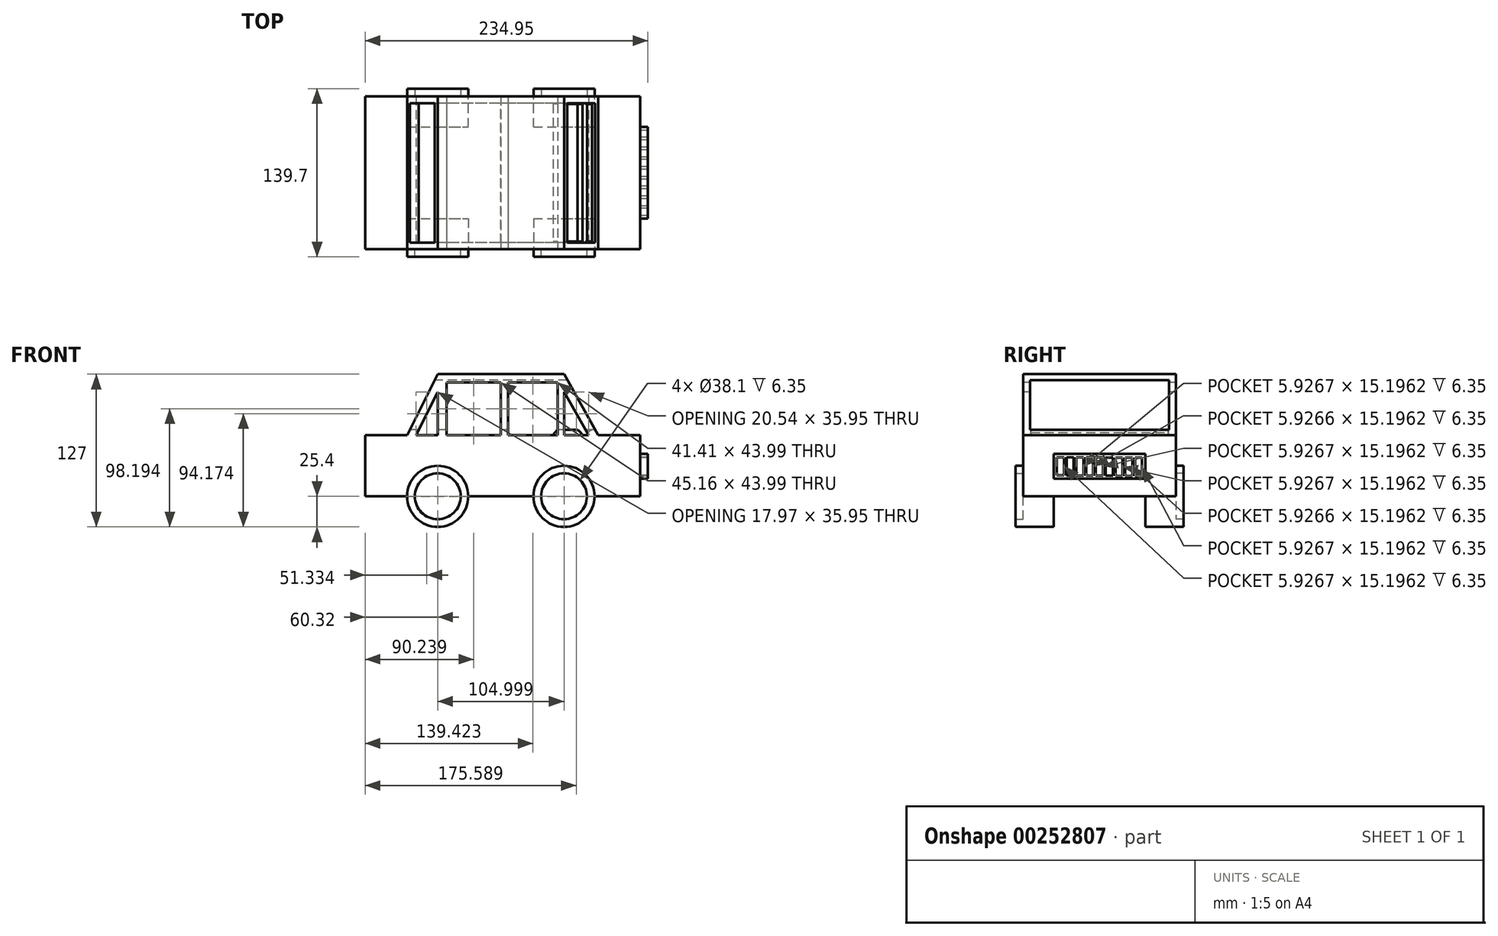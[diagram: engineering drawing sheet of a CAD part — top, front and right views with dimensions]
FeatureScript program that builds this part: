
annotation { "Feature Type Name" : "Feature", "Feature Type Description" : "" }
export const myFeature = defineFeature(function(context is Context, id is Id, definition is map)
    precondition{}
    {
        {
            var Q0;
            Q0=qCreatedBy(makeId("Front.planeOp"),FACE);
            var sketch = newSketch(context, id + "F0", { "sketchPlane" : qUnion([Q0])});
            skLineSegment(sketch, "E0.bottom", {"start": v(-112.82, 27.92) * mm, "end": v(115.78, 27.92) * mm});
            skLineSegment(sketch, "E0.top", {"start": v(-112.82, -22.88) * mm, "end": v(115.78, -22.88) * mm});
            skLineSegment(sketch, "E0.left", {"start": v(-112.82, 27.92) * mm, "end": v(-112.82, -22.88) * mm});
            skLineSegment(sketch, "E0.right", {"start": v(115.78, 27.92) * mm, "end": v(115.78, -22.88) * mm});
            skSolve(sketch);
        }
        {
            var Q0;
            Q0=makeQuery(id+"F0.imprint","IMPRINT",FACE,{"disambiguationData":[TD([[makeQuery(id+"F0.imprint","IMPRINT",EDGE,{"derivedFrom":sQuery(id+"F0.wireOp",EDGE,"E0.bottom")}),-1.0]])]});
            extrude(context, id + "F1", {"entities" : qUnion([Q0]), "endBound" : BoundingType.SYMMETRIC, "depth" : 127 * mm});
        }
        {
            var Q0;
            Q0=makeQuery(id+"F1.opExtrude","CAP_FACE",FACE,{"disambiguationData":[OSD([sQuery(id+"F0.wireOp",EDGE,"E0.bottom"),sQuery(id+"F0.wireOp",EDGE,"E0.top"),sQuery(id+"F0.wireOp",EDGE,"E0.left"),sQuery(id+"F0.wireOp",EDGE,"E0.right")])],"isStart":false});
            var sketch = newSketch(context, id + "F2", { "sketchPlane" : qUnion([Q0])});
            skCircle(sketch, "E1", {"center": v(-52.5, -22.88) * mm, "radius": 25.4 * mm});
            skLineSegment(sketch, "E2", {"start": v(-77.9, -22.88) * mm, "end": v(-112.82, -22.88) * mm});
            skCircle(sketch, "E3.MirrorC", {"center": v(52.5, -22.88) * mm, "radius": 25.4 * mm});
            skSolve(sketch);
        }
        {
            var Q0;
            Q0 = qSketchRegion(id + "F2", true);
            extrude(context, id + "F3", {"entities" : qUnion([Q0]), "operationType" : NewBodyOperationType.ADD, "oppositeDirection" : true, "depth" : 25.4 * mm});
        }
        {
            var Q0;
            Q0=makeQuery(id+"F1.opExtrude","SWEPT_BODY",BODY,{"disambiguationData":[OSD([sQuery(id+"F0.wireOp",EDGE,"E0.bottom"),sQuery(id+"F0.wireOp",EDGE,"E0.top"),sQuery(id+"F0.wireOp",EDGE,"E0.left"),sQuery(id+"F0.wireOp",EDGE,"E0.right")])]});
            var Q1;
            Q1=qCreatedBy(makeId("Front.planeOp"),FACE);
            mirror(context, id + "F4", {"operationType" : NewBodyOperationType.ADD, "entities" : qUnion([Q0]), "mirrorPlane" : qUnion([Q1])});
        }
        {
            var Q0;
            Q0=makeQuery(id+"F1.opExtrude","SWEPT_FACE",FACE,{"disambiguationData":[OSD([sQuery(id+"F0.wireOp",EDGE,"E0.bottom")])]});
            var sketch = newSketch(context, id + "F5", { "sketchPlane" : qUnion([Q0])});
            skLineSegment(sketch, "E4.bottom", {"start": v(-52.5, -63.5) * mm, "end": v(80.85, -63.5) * mm});
            skLineSegment(sketch, "E4.top", {"start": v(-52.5, 63.5) * mm, "end": v(80.85, 63.5) * mm});
            skLineSegment(sketch, "E4.left", {"start": v(-52.5, -63.5) * mm, "end": v(-52.5, 63.5) * mm});
            skLineSegment(sketch, "E4.right", {"start": v(80.85, -63.5) * mm, "end": v(80.85, 63.5) * mm});
            skLineSegment(sketch, "E5", {"start": v(-112.82, -63.5) * mm, "end": v(-52.5, -63.5) * mm});
            skSolve(sketch);
        }
        {
            var Q0;
            Q0 = qSketchRegion(id + "F5", true);
            extrude(context, id + "F6", {"entities" : qUnion([Q0]), "operationType" : NewBodyOperationType.ADD, "depth" : 50.8 * mm});
        }
        {
            var Q0;
            Q0=makeQuery(id+"F6.boolean.opBoolean","MERGE",FACE,{"derivedFrom":[makeQuery(id+"F3.boolean.opBoolean","MERGE",FACE,{"derivedFrom":[makeQuery(id+"F1.opExtrude","CAP_FACE",FACE,{"disambiguationData":[OSD([sQuery(id+"F0.wireOp",EDGE,"E0.bottom"),sQuery(id+"F0.wireOp",EDGE,"E0.top"),sQuery(id+"F0.wireOp",EDGE,"E0.left"),sQuery(id+"F0.wireOp",EDGE,"E0.right")])],"isStart":false}),makeQuery(id+"F3.opExtrude","CAP_FACE",FACE,{"disambiguationData":[OSD([sQuery(id+"F2.wireOp",EDGE,"E1")])],"isStart":true}),makeQuery(id+"F3.opExtrude","CAP_FACE",FACE,{"disambiguationData":[OSD([sQuery(id+"F2.wireOp",EDGE,"E3.MirrorC")])],"isStart":true})]}),makeQuery(id+"F6.opExtrude","SWEPT_FACE",FACE,{"disambiguationData":[OSD([sQuery(id+"F5.wireOp",EDGE,"E4.bottom")])]})]});
            var sketch = newSketch(context, id + "F7", { "sketchPlane" : qUnion([Q0])});
            skPoint(sketch, "E6.endSnap0", {"position": v(52.5, -48.28) * mm});
            skLineSegment(sketch, "E7", {"start": v(52.5, 78.72) * mm, "end": v(80.85, 27.92) * mm});
            skLineSegment(sketch, "E8", {"start": v(80.85, 78.72) * mm, "end": v(52.5, 78.72) * mm});
            skSolve(sketch);
        }
        {
            var Q0;
            Q0=makeQuery(id+"F7.imprint","IMPRINT",FACE,{"disambiguationData":[TD([[makeQuery(id+"F7.imprint","IMPRINT",EDGE,{"derivedFrom":sQuery(id+"F7.wireOp",EDGE,"E7")}),1.0]])]});
            extrude(context, id + "F8", {"entities" : qUnion([Q0]), "operationType" : NewBodyOperationType.REMOVE, "endBound" : BoundingType.THROUGH_ALL, "oppositeDirection" : true, "depth" : 25.4 * mm});
        }
        {
            var Q0;
            Q0=makeQuery(id+"F8.boolean.opBoolean","COPY",FACE,{"derivedFrom":makeQuery(id+"F8.opExtrude","SWEPT_FACE",FACE,{"disambiguationData":[OSD([sQuery(id+"F7.wireOp",EDGE,"E7")])]})});
            var sketch = newSketch(context, id + "F9", { "sketchPlane" : qUnion([Q0])});
            skLineSegment(sketch, "E9.bottom", {"start": v(-57.15, 36.8) * mm, "end": v(57.15, 36.8) * mm});
            skLineSegment(sketch, "E9.top", {"start": v(-57.15, -8.67) * mm, "end": v(57.15, -8.67) * mm});
            skLineSegment(sketch, "E9.left", {"start": v(-57.15, 36.8) * mm, "end": v(-57.15, -8.67) * mm});
            skLineSegment(sketch, "E9.right", {"start": v(57.15, 36.8) * mm, "end": v(57.15, -8.67) * mm});
            skSolve(sketch);
        }
        {
            var Q0;
            Q0=makeQuery(id+"F9.imprint","IMPRINT",FACE,{"disambiguationData":[TD([[makeQuery(id+"F9.imprint","IMPRINT",EDGE,{"derivedFrom":sQuery(id+"F9.wireOp",EDGE,"E9.bottom")}),-1.0]])]});
            extrude(context, id + "F10", {"entities" : qUnion([Q0]), "operationType" : NewBodyOperationType.REMOVE, "oppositeDirection" : true, "depth" : 25.4 * mm});
        }
        {
            var Q0;
            Q0=makeQuery(id+"F6.opExtrude","SWEPT_FACE",FACE,{"disambiguationData":[OSD([sQuery(id+"F5.wireOp",EDGE,"E4.left")])]});
            extrude(context, id + "F11", {"entities" : qUnion([Q0]), "operationType" : NewBodyOperationType.ADD, "depth" : 25.4 * mm});
        }
        {
            var Q0;
            {var subQ0=sQuery(id+"F5.wireOp",EDGE,"E4.bottom");Q0=makeQuery(id+"F11.boolean.opBoolean","MERGE",FACE,{"derivedFrom":[makeQuery(id+"F6.boolean.opBoolean","MERGE",FACE,{"derivedFrom":[makeQuery(id+"F3.boolean.opBoolean","MERGE",FACE,{"derivedFrom":[makeQuery(id+"F1.opExtrude","CAP_FACE",FACE,{"disambiguationData":[OSD([sQuery(id+"F0.wireOp",EDGE,"E0.bottom"),sQuery(id+"F0.wireOp",EDGE,"E0.top"),sQuery(id+"F0.wireOp",EDGE,"E0.left"),sQuery(id+"F0.wireOp",EDGE,"E0.right")])],"isStart":false}),makeQuery(id+"F3.opExtrude","CAP_FACE",FACE,{"disambiguationData":[OSD([sQuery(id+"F2.wireOp",EDGE,"E1")])],"isStart":true}),makeQuery(id+"F3.opExtrude","CAP_FACE",FACE,{"disambiguationData":[OSD([sQuery(id+"F2.wireOp",EDGE,"E3.MirrorC")])],"isStart":true})]}),makeQuery(id+"F6.opExtrude","SWEPT_FACE",FACE,{"disambiguationData":[OSD([subQ0])]})]}),makeQuery(id+"F11.opExtrude","SWEPT_FACE",FACE,{"disambiguationData":[OSD([subQ0,sQuery(id+"F5.wireOp",EDGE,"E4.left"),sQuery(id+"F5.wireOp",EDGE,"E5")])]})]});}
            var sketch = newSketch(context, id + "F12", { "sketchPlane" : qUnion([Q0])});
            skLineSegment(sketch, "E10", {"start": v(-77.9, 27.92) * mm, "end": v(-77.9, 78.72) * mm});
            skLineSegment(sketch, "E11", {"start": v(-77.9, 78.72) * mm, "end": v(-52.5, 78.72) * mm});
            skPoint(sketch, "E11.endSnap0", {"position": v(-52.5, -48.28) * mm});
            skLineSegment(sketch, "E12", {"start": v(-52.5, 78.72) * mm, "end": v(-77.9, 27.92) * mm});
            skSolve(sketch);
        }
        {
            var Q0;
            Q0=makeQuery(id+"F12.imprint","IMPRINT",FACE,{"disambiguationData":[TD([[makeQuery(id+"F12.imprint","IMPRINT",EDGE,{"derivedFrom":sQuery(id+"F12.wireOp",EDGE,"E10")}),1.0]])]});
            extrude(context, id + "F13", {"entities" : qUnion([Q0]), "operationType" : NewBodyOperationType.REMOVE, "endBound" : BoundingType.THROUGH_ALL, "oppositeDirection" : true, "depth" : 25.4 * mm});
        }
        {
            var Q0;
            {var subQ0=sQuery(id+"F5.wireOp",EDGE,"E4.bottom");Q0=makeQuery(id+"F11.boolean.opBoolean","MERGE",FACE,{"derivedFrom":[makeQuery(id+"F6.boolean.opBoolean","MERGE",FACE,{"derivedFrom":[makeQuery(id+"F3.boolean.opBoolean","MERGE",FACE,{"derivedFrom":[makeQuery(id+"F1.opExtrude","CAP_FACE",FACE,{"disambiguationData":[OSD([sQuery(id+"F0.wireOp",EDGE,"E0.bottom"),sQuery(id+"F0.wireOp",EDGE,"E0.top"),sQuery(id+"F0.wireOp",EDGE,"E0.left"),sQuery(id+"F0.wireOp",EDGE,"E0.right")])],"isStart":false}),makeQuery(id+"F3.opExtrude","CAP_FACE",FACE,{"disambiguationData":[OSD([sQuery(id+"F2.wireOp",EDGE,"E1")])],"isStart":true}),makeQuery(id+"F3.opExtrude","CAP_FACE",FACE,{"disambiguationData":[OSD([sQuery(id+"F2.wireOp",EDGE,"E3.MirrorC")])],"isStart":true})]}),makeQuery(id+"F6.opExtrude","SWEPT_FACE",FACE,{"disambiguationData":[OSD([subQ0])]})]}),makeQuery(id+"F11.opExtrude","SWEPT_FACE",FACE,{"disambiguationData":[OSD([subQ0,sQuery(id+"F5.wireOp",EDGE,"E4.left"),sQuery(id+"F5.wireOp",EDGE,"E5")])]})]});}
            var sketch = newSketch(context, id + "F14", { "sketchPlane" : qUnion([Q0])});
            skLineSegment(sketch, "E13", {"start": v(-52.5, 63.87) * mm, "end": v(-70.47, 27.92) * mm});
            skLineSegment(sketch, "E14", {"start": v(-70.47, 27.92) * mm, "end": v(-52.5, 27.92) * mm});
            skLineSegment(sketch, "E15", {"start": v(-52.5, 27.92) * mm, "end": v(-52.5, 63.87) * mm});
            skLineSegment(sketch, "E16", {"start": v(-45.16, 71.9) * mm, "end": v(-45.16, 27.92) * mm});
            skLineSegment(sketch, "E17", {"start": v(-45.16, 27.92) * mm, "end": v(0, 27.92) * mm});
            skLineSegment(sketch, "E18", {"start": v(0, 27.92) * mm, "end": v(0, 71.9) * mm});
            skLineSegment(sketch, "E19", {"start": v(0, 71.9) * mm, "end": v(-45.16, 71.9) * mm});
            skLineSegment(sketch, "E20", {"start": v(5.9, 71.9) * mm, "end": v(5.9, 27.92) * mm});
            skLineSegment(sketch, "E21", {"start": v(5.9, 27.92) * mm, "end": v(47.3, 27.92) * mm});
            skLineSegment(sketch, "E22", {"start": v(47.3, 27.92) * mm, "end": v(47.3, 71.9) * mm});
            skLineSegment(sketch, "E23", {"start": v(47.3, 71.9) * mm, "end": v(5.9, 71.9) * mm});
            skLineSegment(sketch, "E24", {"start": v(52.5, 63.87) * mm, "end": v(52.5, 27.92) * mm});
            skLineSegment(sketch, "E25", {"start": v(52.5, 63.87) * mm, "end": v(73.04, 27.92) * mm});
            skLineSegment(sketch, "E26", {"start": v(73.04, 27.92) * mm, "end": v(52.5, 27.92) * mm});
            skSolve(sketch);
        }
        {
            var Q0;
            Q0 = qSketchRegion(id + "F14", true);
            extrude(context, id + "F15", {"entities" : qUnion([Q0]), "operationType" : NewBodyOperationType.REMOVE, "endBound" : BoundingType.THROUGH_ALL, "oppositeDirection" : true, "depth" : 6.35 * mm});
        }
        {
            var Q0;
            {var subQ2=sQuery(id+"F9.wireOp",EDGE,"E9.top");Q0=makeQuery(id+"F15.boolean.opBoolean","SPLIT",FACE,{"disambiguationData":[TD([makeQuery(id+"F15.opExtrude","SWEPT_FACE",FACE,{"disambiguationData":[OSD([sQuery(id+"F14.wireOp",EDGE,"E26")])]})])],"derivedFrom":makeQuery(id+"F10.boolean.opBoolean","COPY",FACE,{"derivedFrom":makeQuery(id+"F10.opExtrude","SWEPT_FACE",FACE,{"disambiguationData":[OSD([subQ2])]})})});}
            var Q1;
            Q1=makeQuery(id+"F10.boolean.opBoolean","COPY",EDGE,{"derivedFrom":makeQuery(id+"F10.opExtrude","CAP_EDGE",EDGE,{"disambiguationData":[OSD([sQuery(id+"F9.wireOp",EDGE,"E9.top")])],"isStart":false})});
            revolve(context, id + "F16", {"operationType" : NewBodyOperationType.ADD, "entities" : qUnion([Q0]), "axis" : qUnion([Q1]), "revolveType" : RevolveType.FULL});
        }
        {
            var Q0;
            Q0=qCreatedBy(makeId("Right.planeOp"),FACE);
            cPlane(context, id + "F17", {"entities" : qUnion([Q0]), "cplaneType" : CPlaneType.OFFSET, "offset" : 76.2 * mm, "oppositeDirection" : true, "width" : 152.4 * mm, "height" : 152.4 * mm});
        }
        {
            var Q0;
            Q0=qCreatedBy(id+"F17.planeOp",FACE);
            var sketch = newSketch(context, id + "F18", { "sketchPlane" : qUnion([Q0])});
            skLineSegment(sketch, "E27.bottom", {"start": v(57.93, 73.69) * mm, "end": v(-57.93, 73.69) * mm});
            skLineSegment(sketch, "E27.top", {"start": v(57.93, 32.37) * mm, "end": v(-57.93, 32.37) * mm});
            skLineSegment(sketch, "E27.left", {"start": v(57.93, 73.69) * mm, "end": v(57.93, 32.37) * mm});
            skLineSegment(sketch, "E27.right", {"start": v(-57.93, 73.69) * mm, "end": v(-57.93, 32.37) * mm});
            skSolve(sketch);
        }
        {
            var Q0;
            Q0=makeQuery(id+"F18.imprint","IMPRINT",FACE,{"disambiguationData":[TD([[makeQuery(id+"F18.imprint","IMPRINT",EDGE,{"derivedFrom":sQuery(id+"F18.wireOp",EDGE,"E27.bottom")}),1.0]])]});
            extrude(context, id + "F19", {"entities" : qUnion([Q0]), "operationType" : NewBodyOperationType.REMOVE, "endBound" : BoundingType.THROUGH_ALL, "depth" : 25.4 * mm});
        }
        {
            var Q0;
            Q0=makeQuery(id+"F1.opExtrude","SWEPT_FACE",FACE,{"disambiguationData":[OSD([sQuery(id+"F0.wireOp",EDGE,"E0.right")])]});
            var sketch = newSketch(context, id + "F20", { "sketchPlane" : qUnion([Q0])});
            skLineSegment(sketch, "E28.bottom", {"start": v(-38.1, 12.41) * mm, "end": v(38.1, 12.41) * mm});
            skLineSegment(sketch, "E28.top", {"start": v(-38.1, -8.22) * mm, "end": v(38.1, -8.22) * mm});
            skLineSegment(sketch, "E28.left", {"start": v(-38.1, 12.41) * mm, "end": v(-38.1, -8.22) * mm});
            skLineSegment(sketch, "E28.right", {"start": v(38.1, 12.41) * mm, "end": v(38.1, -8.22) * mm});
            skLineSegment(sketch, "E29.bottom", {"start": v(-35.56, 9.72) * mm, "end": v(-29.63, 9.72) * mm});
            skLineSegment(sketch, "E29.top", {"start": v(-35.56, -5.48) * mm, "end": v(-29.63, -5.48) * mm});
            skLineSegment(sketch, "E29.left", {"start": v(-35.56, 9.72) * mm, "end": v(-35.56, -5.48) * mm});
            skLineSegment(sketch, "E29.right", {"start": v(-29.63, 9.72) * mm, "end": v(-29.63, -5.48) * mm});
            skLineSegment(sketch, "E30.1.0.0", {"start": v(-27.43, 9.65) * mm, "end": v(-21.5, 9.65) * mm});
            skLineSegment(sketch, "E30.1.0.1", {"start": v(-21.5, 9.65) * mm, "end": v(-21.5, -5.54) * mm});
            skLineSegment(sketch, "E30.1.0.2", {"start": v(-27.43, 9.65) * mm, "end": v(-27.43, -5.54) * mm});
            skLineSegment(sketch, "E30.1.0.3", {"start": v(-27.43, -5.54) * mm, "end": v(-21.5, -5.54) * mm});
            skLineSegment(sketch, "E30.2.0.0", {"start": v(-19.3, 9.59) * mm, "end": v(-13.38, 9.59) * mm});
            skLineSegment(sketch, "E30.2.0.1", {"start": v(-13.38, 9.59) * mm, "end": v(-13.38, -5.6) * mm});
            skLineSegment(sketch, "E30.2.0.2", {"start": v(-19.3, 9.59) * mm, "end": v(-19.3, -5.6) * mm});
            skLineSegment(sketch, "E30.2.0.3", {"start": v(-19.3, -5.6) * mm, "end": v(-13.38, -5.6) * mm});
            skLineSegment(sketch, "E30.3.0.0", {"start": v(-11.18, 9.53) * mm, "end": v(-5.25, 9.53) * mm});
            skLineSegment(sketch, "E30.3.0.1", {"start": v(-5.25, 9.53) * mm, "end": v(-5.25, -5.67) * mm});
            skLineSegment(sketch, "E30.3.0.2", {"start": v(-11.18, 9.53) * mm, "end": v(-11.18, -5.67) * mm});
            skLineSegment(sketch, "E30.3.0.3", {"start": v(-11.18, -5.67) * mm, "end": v(-5.25, -5.67) * mm});
            skLineSegment(sketch, "E30.4.0.0", {"start": v(-3.05, 9.46) * mm, "end": v(2.88, 9.46) * mm});
            skLineSegment(sketch, "E30.4.0.1", {"start": v(2.88, 9.46) * mm, "end": v(2.88, -5.73) * mm});
            skLineSegment(sketch, "E30.4.0.2", {"start": v(-3.05, 9.46) * mm, "end": v(-3.05, -5.73) * mm});
            skLineSegment(sketch, "E30.4.0.3", {"start": v(-3.05, -5.73) * mm, "end": v(2.88, -5.73) * mm});
            skLineSegment(sketch, "E30.5.0.0", {"start": v(5.08, 9.4) * mm, "end": v(11, 9.4) * mm});
            skLineSegment(sketch, "E30.5.0.1", {"start": v(11, 9.4) * mm, "end": v(11, -5.8) * mm});
            skLineSegment(sketch, "E30.5.0.2", {"start": v(5.08, 9.4) * mm, "end": v(5.08, -5.8) * mm});
            skLineSegment(sketch, "E30.5.0.3", {"start": v(5.08, -5.8) * mm, "end": v(11, -5.8) * mm});
            skLineSegment(sketch, "E30.6.0.0", {"start": v(13.2, 9.33) * mm, "end": v(19.13, 9.33) * mm});
            skLineSegment(sketch, "E30.6.0.1", {"start": v(19.13, 9.33) * mm, "end": v(19.13, -5.86) * mm});
            skLineSegment(sketch, "E30.6.0.2", {"start": v(13.2, 9.33) * mm, "end": v(13.2, -5.86) * mm});
            skLineSegment(sketch, "E30.6.0.3", {"start": v(13.2, -5.86) * mm, "end": v(19.13, -5.86) * mm});
            skLineSegment(sketch, "E30.7.0.0", {"start": v(21.33, 9.27) * mm, "end": v(27.26, 9.27) * mm});
            skLineSegment(sketch, "E30.7.0.1", {"start": v(27.26, 9.27) * mm, "end": v(27.26, -5.93) * mm});
            skLineSegment(sketch, "E30.7.0.2", {"start": v(21.33, 9.27) * mm, "end": v(21.33, -5.93) * mm});
            skLineSegment(sketch, "E30.7.0.3", {"start": v(21.33, -5.93) * mm, "end": v(27.26, -5.93) * mm});
            skLineSegment(sketch, "E30.8.0.0", {"start": v(29.46, 9.2) * mm, "end": v(35.39, 9.2) * mm});
            skLineSegment(sketch, "E30.8.0.1", {"start": v(35.39, 9.2) * mm, "end": v(35.39, -5.99) * mm});
            skLineSegment(sketch, "E30.8.0.2", {"start": v(29.46, 9.2) * mm, "end": v(29.46, -5.99) * mm});
            skLineSegment(sketch, "E30.8.0.3", {"start": v(29.46, -5.99) * mm, "end": v(35.39, -5.99) * mm});
            skLineSegment(sketch, "E30.direction1", {"start": v(-35.56, 9.72) * mm, "end": v(-27.43, 9.65) * mm, "construction": true});
            skPoint(sketch, "E31.centerSnap0", {"position": v(5.08, 1.8) * mm});
            skPoint(sketch, "E32.middle", {"position": v(0, 4.99) * mm});
            skSolve(sketch);
        }
        {
            var Q0;
            Q0=makeQuery(id+"F20.imprint","IMPRINT",FACE,{"disambiguationData":[TD([[makeQuery(id+"F20.imprint","IMPRINT",EDGE,{"derivedFrom":sQuery(id+"F20.wireOp",EDGE,"E28.bottom")}),-1.0]])]});
            extrude(context, id + "F21", {"entities" : qUnion([Q0]), "operationType" : NewBodyOperationType.ADD, "depth" : 6.35 * mm});
        }
        {
            var Q0;
            {var subQ0=sQuery(id+"F5.wireOp",EDGE,"E4.top");var subQ1=sQuery(id+"F0.wireOp",EDGE,"E0.bottom");var subQ2=sQuery(id+"F0.wireOp",EDGE,"E0.right");var subQ3=sQuery(id+"F0.wireOp",EDGE,"E0.left");var subQ4=sQuery(id+"F0.wireOp",EDGE,"E0.top");Q0=makeQuery(id+"F11.boolean.opBoolean","MERGE",FACE,{"derivedFrom":[makeQuery(id+"F6.boolean.opBoolean","MERGE",FACE,{"derivedFrom":[makeQuery(id+"F4.boolean.opBoolean","MERGE",FACE,{"derivedFrom":[makeQuery(id+"F1.opExtrude","CAP_FACE",FACE,{"disambiguationData":[OSD([subQ1,subQ4,subQ3,subQ2])],"isStart":true}),makeQuery(id+"F4.opPattern","COPY",FACE,{"derivedFrom":makeQuery(id+"F3.boolean.opBoolean","MERGE",FACE,{"derivedFrom":[makeQuery(id+"F1.opExtrude","CAP_FACE",FACE,{"disambiguationData":[OSD([subQ1,subQ4,subQ3,subQ2])],"isStart":false}),makeQuery(id+"F3.opExtrude","CAP_FACE",FACE,{"disambiguationData":[OSD([sQuery(id+"F2.wireOp",EDGE,"E1")])],"isStart":true}),makeQuery(id+"F3.opExtrude","CAP_FACE",FACE,{"disambiguationData":[OSD([sQuery(id+"F2.wireOp",EDGE,"E3.MirrorC")])],"isStart":true})]}),"instanceName":"1"})]}),makeQuery(id+"F6.opExtrude","SWEPT_FACE",FACE,{"disambiguationData":[OSD([subQ0])]})]}),makeQuery(id+"F11.opExtrude","SWEPT_FACE",FACE,{"disambiguationData":[OSD([subQ1,subQ0,sQuery(id+"F5.wireOp",EDGE,"E4.left")])]})]});}
            var sketch = newSketch(context, id + "F22", { "sketchPlane" : qUnion([Q0])});
            skCircle(sketch, "E33", {"center": v(-52.5, -22.88) * mm, "radius": 25.4 * mm});
            skPoint(sketch, "E33.first.point", {"position": v(-77.9, -22.88) * mm});
            skPoint(sketch, "E33.second.point", {"position": v(-27.1, -22.88) * mm});
            skPoint(sketch, "E33.third.point", {"position": v(-52.5, -48.28) * mm});
            skCircle(sketch, "E34", {"center": v(52.5, -22.88) * mm, "radius": 25.4 * mm});
            skPoint(sketch, "E34.first.point", {"position": v(27.1, -22.88) * mm});
            skPoint(sketch, "E34.second.point", {"position": v(77.9, -22.88) * mm});
            skPoint(sketch, "E34.third.point", {"position": v(52.5, -48.28) * mm});
            skCircle(sketch, "E35", {"center": v(-52.5, -22.88) * mm, "radius": 19.05 * mm});
            skCircle(sketch, "E36", {"center": v(52.5, -22.88) * mm, "radius": 19.05 * mm});
            skSolve(sketch);
        }
        {
            var Q0;
            {var subQ0=sQuery(id+"F22.wireOp",EDGE,"E34");Q0=makeQuery(id+"F22.imprint","IMPRINT",FACE,{"disambiguationData":[TD([[makeQuery(id+"F22.imprint","IMPRINT",EDGE,{"disambiguationData":[OD(0.0)],"derivedFrom":subQ0}),1.0]])]});}
            var Q1;
            Q1=makeQuery(id+"F22.imprint","IMPRINT",FACE,{"disambiguationData":[TD([[makeQuery(id+"F22.imprint","IMPRINT",EDGE,{"derivedFrom":sQuery(id+"F22.wireOp",EDGE,"E35")}),-1.0]])]});
            extrude(context, id + "F23", {"entities" : qUnion([Q0, Q1]), "operationType" : NewBodyOperationType.ADD, "depth" : 6.35 * mm});
        }
        {
            var Q0;
            {var subQ0=sQuery(id+"F5.wireOp",EDGE,"E4.bottom");Q0=makeQuery(id+"F11.boolean.opBoolean","MERGE",FACE,{"derivedFrom":[makeQuery(id+"F6.boolean.opBoolean","MERGE",FACE,{"derivedFrom":[makeQuery(id+"F3.boolean.opBoolean","MERGE",FACE,{"derivedFrom":[makeQuery(id+"F1.opExtrude","CAP_FACE",FACE,{"disambiguationData":[OSD([sQuery(id+"F0.wireOp",EDGE,"E0.bottom"),sQuery(id+"F0.wireOp",EDGE,"E0.top"),sQuery(id+"F0.wireOp",EDGE,"E0.left"),sQuery(id+"F0.wireOp",EDGE,"E0.right")])],"isStart":false}),makeQuery(id+"F3.opExtrude","CAP_FACE",FACE,{"disambiguationData":[OSD([sQuery(id+"F2.wireOp",EDGE,"E1")])],"isStart":true}),makeQuery(id+"F3.opExtrude","CAP_FACE",FACE,{"disambiguationData":[OSD([sQuery(id+"F2.wireOp",EDGE,"E3.MirrorC")])],"isStart":true})]}),makeQuery(id+"F6.opExtrude","SWEPT_FACE",FACE,{"disambiguationData":[OSD([subQ0])]})]}),makeQuery(id+"F11.opExtrude","SWEPT_FACE",FACE,{"disambiguationData":[OSD([subQ0,sQuery(id+"F5.wireOp",EDGE,"E4.left"),sQuery(id+"F5.wireOp",EDGE,"E5")])]})]});}
            var sketch = newSketch(context, id + "F24", { "sketchPlane" : qUnion([Q0])});
            skCircle(sketch, "E37", {"center": v(-52.5, -22.88) * mm, "radius": 25.4 * mm});
            skPoint(sketch, "E37.first.point", {"position": v(-77.9, -22.88) * mm});
            skPoint(sketch, "E37.second.point", {"position": v(-27.1, -22.88) * mm});
            skPoint(sketch, "E37.third.point", {"position": v(-52.5, -48.28) * mm});
            skCircle(sketch, "E38", {"center": v(52.5, -22.88) * mm, "radius": 25.4 * mm});
            skPoint(sketch, "E38.first.point", {"position": v(27.1, -22.88) * mm});
            skPoint(sketch, "E38.second.point", {"position": v(77.9, -22.88) * mm});
            skPoint(sketch, "E38.third.point", {"position": v(52.5, -48.28) * mm});
            skCircle(sketch, "E39", {"center": v(-52.5, -22.88) * mm, "radius": 19.05 * mm});
            skCircle(sketch, "E40", {"center": v(52.5, -22.88) * mm, "radius": 19.05 * mm});
            skSolve(sketch);
        }
        {
            var Q0;
            Q0=makeQuery(id+"F24.imprint","IMPRINT",FACE,{"disambiguationData":[TD([[makeQuery(id+"F24.imprint","IMPRINT",EDGE,{"derivedFrom":sQuery(id+"F24.wireOp",EDGE,"E39")}),-1.0]])]});
            var Q1;
            {var subQ0=sQuery(id+"F24.wireOp",EDGE,"E38");Q1=makeQuery(id+"F24.imprint","IMPRINT",FACE,{"disambiguationData":[TD([[makeQuery(id+"F24.imprint","IMPRINT",EDGE,{"disambiguationData":[OD(0.0)],"derivedFrom":subQ0}),1.0]])]});}
            extrude(context, id + "F25", {"entities" : qUnion([Q0, Q1]), "operationType" : NewBodyOperationType.ADD, "depth" : 6.35 * mm});
        }
    });
